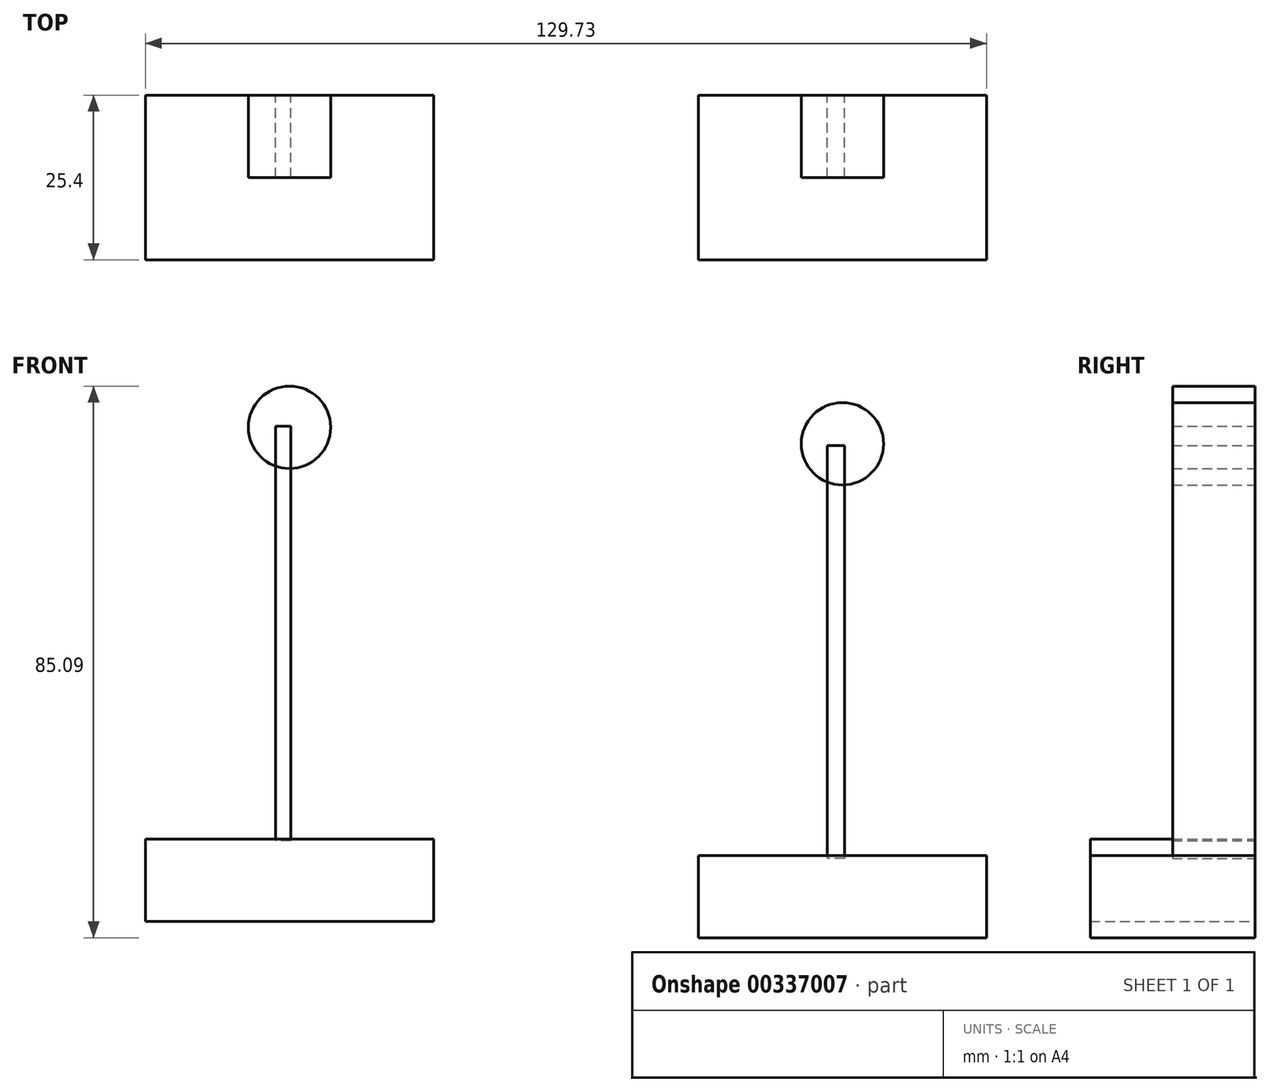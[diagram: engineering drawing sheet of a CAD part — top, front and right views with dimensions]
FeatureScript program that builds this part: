
annotation { "Feature Type Name" : "Feature", "Feature Type Description" : "" }
export const myFeature = defineFeature(function(context is Context, id is Id, definition is map)
    precondition{}
    {
        {
            var Q0;
            Q0=qCreatedBy(makeId("Front.planeOp"),FACE);
            var sketch = newSketch(context, id + "F0", { "sketchPlane" : qUnion([Q0])});
            skLineSegment(sketch, "E0.bottom", {"start": v(-69.4, -21.66) * mm, "end": v(-24.96, -21.66) * mm});
            skLineSegment(sketch, "E0.top", {"start": v(-69.4, -34.36) * mm, "end": v(-24.96, -34.36) * mm});
            skLineSegment(sketch, "E0.left", {"start": v(-69.4, -21.66) * mm, "end": v(-69.4, -34.36) * mm});
            skLineSegment(sketch, "E0.right", {"start": v(-24.96, -21.66) * mm, "end": v(-24.96, -34.36) * mm});
            skLineSegment(sketch, "E1.bottom", {"start": v(15.87, -24.2) * mm, "end": v(60.32, -24.2) * mm});
            skLineSegment(sketch, "E1.top", {"start": v(15.87, -36.9) * mm, "end": v(60.32, -36.9) * mm});
            skLineSegment(sketch, "E1.left", {"start": v(15.87, -24.2) * mm, "end": v(15.87, -36.9) * mm});
            skLineSegment(sketch, "E1.right", {"start": v(60.32, -24.2) * mm, "end": v(60.32, -36.9) * mm});
            skLineSegment(sketch, "E2", {"start": v(-47.18, -21.66) * mm, "end": v(-47.18, 41.84) * mm});
            skLineSegment(sketch, "E3", {"start": v(38.1, -24.2) * mm, "end": v(38.1, 39.3) * mm});
            skCircle(sketch, "E4", {"center": v(-47.18, 41.84) * mm, "radius": 6.35 * mm});
            skCircle(sketch, "E5", {"center": v(38.1, 39.3) * mm, "radius": 6.35 * mm});
            skSolve(sketch);
        }
        {
            var Q0;
            Q0=makeQuery(id+"F0.imprint","IMPRINT",FACE,{"disambiguationData":[TD([[makeQuery(id+"F0.imprint","IMPRINT",EDGE,{"derivedFrom":sQuery(id+"F0.wireOp",EDGE,"E0.top")}),1.0]])]});
            var Q1;
            Q1=makeQuery(id+"F0.imprint","IMPRINT",FACE,{"disambiguationData":[TD([[makeQuery(id+"F0.imprint","IMPRINT",EDGE,{"derivedFrom":sQuery(id+"F0.wireOp",EDGE,"E1.top")}),1.0]])]});
            extrude(context, id + "F1", {"entities" : qUnion([Q0, Q1]), "depth" : 25.4 * mm});
        }
        {
            var Q0;
            Q0=makeQuery(id+"F0.imprint","IMPRINT",FACE,{"disambiguationData":[TD([[makeQuery(id+"F0.imprint","IMPRINT",EDGE,{"derivedFrom":sQuery(id+"F0.wireOp",EDGE,"E5")}),1.0]])]});
            var Q1;
            Q1=makeQuery(id+"F0.imprint","IMPRINT",FACE,{"disambiguationData":[TD([[makeQuery(id+"F0.imprint","IMPRINT",EDGE,{"derivedFrom":sQuery(id+"F0.wireOp",EDGE,"E4")}),1.0]])]});
            extrude(context, id + "F2", {"entities" : qUnion([Q0, Q1]), "depth" : 12.7 * mm});
        }
        {
            var Q0;
            Q0=qCreatedBy(makeId("Front.planeOp"),FACE);
            var sketch = newSketch(context, id + "F3", { "sketchPlane" : qUnion([Q0])});
            skLineSegment(sketch, "E6.bottom", {"start": v(38.41, 39) * mm, "end": v(35.76, 39) * mm});
            skLineSegment(sketch, "E6.top", {"start": v(38.41, -24.68) * mm, "end": v(35.76, -24.68) * mm});
            skLineSegment(sketch, "E6.left", {"start": v(38.41, 39) * mm, "end": v(38.41, -24.68) * mm});
            skLineSegment(sketch, "E6.right", {"start": v(35.76, 39) * mm, "end": v(35.76, -24.68) * mm});
            skLineSegment(sketch, "E7.bottom", {"start": v(-46.98, 42) * mm, "end": v(-49.34, 42) * mm});
            skLineSegment(sketch, "E7.top", {"start": v(-46.98, -21.95) * mm, "end": v(-49.34, -21.95) * mm});
            skLineSegment(sketch, "E7.left", {"start": v(-46.98, 42) * mm, "end": v(-46.98, -21.95) * mm});
            skLineSegment(sketch, "E7.right", {"start": v(-49.34, 42) * mm, "end": v(-49.34, -21.95) * mm});
            skSolve(sketch);
        }
        {
            var Q0;
            Q0=makeQuery(id+"F3.imprint","IMPRINT",FACE,{"disambiguationData":[TD([[makeQuery(id+"F3.imprint","IMPRINT",EDGE,{"derivedFrom":sQuery(id+"F3.wireOp",EDGE,"E6.bottom")}),1.0]])]});
            var Q1;
            Q1=makeQuery(id+"F3.imprint","IMPRINT",FACE,{"disambiguationData":[TD([[makeQuery(id+"F3.imprint","IMPRINT",EDGE,{"derivedFrom":sQuery(id+"F3.wireOp",EDGE,"E7.bottom")}),1.0]])]});
            extrude(context, id + "F4", {"entities" : qUnion([Q0, Q1]), "depth" : 12.7 * mm});
        }
    });
